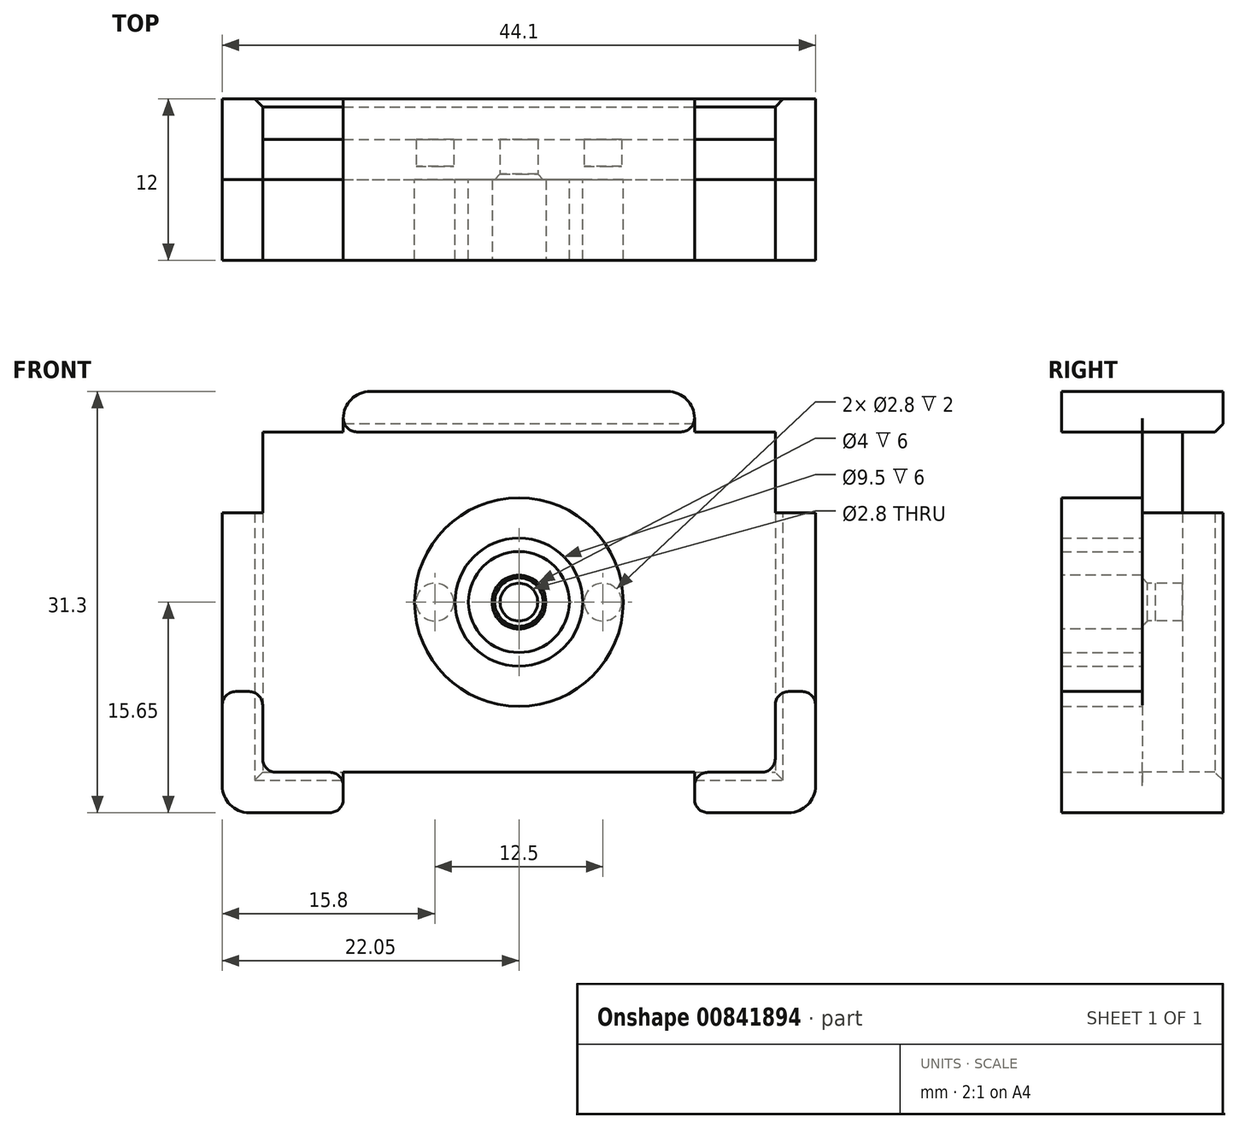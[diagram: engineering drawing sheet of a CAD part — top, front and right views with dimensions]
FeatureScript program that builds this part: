
annotation { "Feature Type Name" : "Feature", "Feature Type Description" : "" }
export const myFeature = defineFeature(function(context is Context, id is Id, definition is map)
    precondition{}
    {
        {
            var Q0;
            Q0=qCreatedBy(makeId("Front.planeOp"),FACE);
            var sketch = newSketch(context, id + "F0", { "sketchPlane" : qUnion([Q0])});
            skLineSegment(sketch, "E0.bottom", {"start": v(-19.05, 12.65) * mm, "end": v(19.05, 12.65) * mm});
            skLineSegment(sketch, "E0.top", {"start": v(-19.05, -12.65) * mm, "end": v(19.05, -12.65) * mm});
            skLineSegment(sketch, "E0.left", {"start": v(-19.05, 12.65) * mm, "end": v(-19.05, -12.65) * mm});
            skLineSegment(sketch, "E0.right", {"start": v(19.05, 12.65) * mm, "end": v(19.05, -12.65) * mm});
            skPoint(sketch, "E0.middle", {"position": v(0, 0) * mm});
            skLineSegment(sketch, "E1.bottom", {"start": v(-22.05, 15.65) * mm, "end": v(22.05, 15.65) * mm});
            skLineSegment(sketch, "E1.top", {"start": v(-22.05, -15.65) * mm, "end": v(22.05, -15.65) * mm});
            skLineSegment(sketch, "E1.left", {"start": v(-22.05, 15.65) * mm, "end": v(-22.05, -15.65) * mm});
            skLineSegment(sketch, "E1.right", {"start": v(22.05, 15.65) * mm, "end": v(22.05, -15.65) * mm});
            skCircle(sketch, "E2", {"center": v(-6.25, 0) * mm, "radius": 1.4 * mm});
            skCircle(sketch, "E3", {"center": v(6.25, 0) * mm, "radius": 1.4 * mm});
            skCircle(sketch, "E4", {"center": v(0, 0) * mm, "radius": 2 * mm});
            skCircle(sketch, "E5", {"center": v(0, 0) * mm, "radius": 4.75 * mm});
            skCircle(sketch, "E6", {"center": v(0, 0) * mm, "radius": 3.75 * mm});
            skCircle(sketch, "E7", {"center": v(0, 0) * mm, "radius": 9.5 * mm});
            skCircle(sketch, "E8", {"center": v(0, 0) * mm, "radius": 7.75 * mm});
            skCircle(sketch, "E9", {"center": v(0, 0) * mm, "radius": 1.4 * mm});
            skLineSegment(sketch, "E10.bottom", {"start": v(-13.05, -12.65) * mm, "end": v(13.05, -12.65) * mm});
            skLineSegment(sketch, "E10.top", {"start": v(-13.05, -15.65) * mm, "end": v(13.05, -15.65) * mm});
            skLineSegment(sketch, "E10.left", {"start": v(-13.05, -12.65) * mm, "end": v(-13.05, -15.65) * mm});
            skLineSegment(sketch, "E10.right", {"start": v(13.05, -12.65) * mm, "end": v(13.05, -15.65) * mm});
            skLineSegment(sketch, "E11.bottom", {"start": v(-13.05, 15.65) * mm, "end": v(13.05, 15.65) * mm});
            skLineSegment(sketch, "E11.top", {"start": v(-13.05, 12.65) * mm, "end": v(13.05, 12.65) * mm});
            skLineSegment(sketch, "E11.left", {"start": v(-13.05, 15.65) * mm, "end": v(-13.05, 12.65) * mm});
            skLineSegment(sketch, "E11.right", {"start": v(13.05, 15.65) * mm, "end": v(13.05, 12.65) * mm});
            skLineSegment(sketch, "E12.bottom", {"start": v(-22.05, -6.65) * mm, "end": v(-19.05, -6.65) * mm});
            skLineSegment(sketch, "E12.top", {"start": v(-22.05, 6.65) * mm, "end": v(-19.05, 6.65) * mm});
            skLineSegment(sketch, "E12.left", {"start": v(-22.05, -6.65) * mm, "end": v(-22.05, 6.65) * mm});
            skLineSegment(sketch, "E12.right", {"start": v(-19.05, -6.65) * mm, "end": v(-19.05, 6.65) * mm});
            skLineSegment(sketch, "E13.bottom", {"start": v(19.05, 6.65) * mm, "end": v(22.05, 6.65) * mm});
            skLineSegment(sketch, "E13.top", {"start": v(19.05, -6.65) * mm, "end": v(22.05, -6.65) * mm});
            skLineSegment(sketch, "E13.left", {"start": v(19.05, 6.65) * mm, "end": v(19.05, -6.65) * mm});
            skLineSegment(sketch, "E13.right", {"start": v(22.05, 6.65) * mm, "end": v(22.05, -6.65) * mm});
            skSolve(sketch);
        }
        {
            var Q0;
            Q0=makeQuery(id+"F0.imprint","IMPRINT",FACE,{"disambiguationData":[TD([[makeQuery(id+"F0.imprint","IMPRINT",EDGE,{"derivedFrom":sQuery(id+"F0.wireOp",EDGE,"E0.bottom")}),-1.0]])]});
            var Q1;
            Q1=makeQuery(id+"F0.imprint","IMPRINT",FACE,{"disambiguationData":[TD([[makeQuery(id+"F0.imprint","IMPRINT",EDGE,{"derivedFrom":sQuery(id+"F0.wireOp",EDGE,"E4")}),-1.0]])]});
            var Q2;
            Q2=makeQuery(id+"F0.imprint","IMPRINT",FACE,{"disambiguationData":[TD([[makeQuery(id+"F0.imprint","IMPRINT",EDGE,{"derivedFrom":sQuery(id+"F0.wireOp",EDGE,"E5")}),1.0]])]});
            var Q3;
            Q3=makeQuery(id+"F0.imprint","IMPRINT",FACE,{"disambiguationData":[TD([[makeQuery(id+"F0.imprint","IMPRINT",EDGE,{"derivedFrom":sQuery(id+"F0.wireOp",EDGE,"E2")}),-1.0]])]});
            var Q4;
            Q4=makeQuery(id+"F0.imprint","IMPRINT",FACE,{"disambiguationData":[TD([[makeQuery(id+"F0.imprint","IMPRINT",EDGE,{"derivedFrom":sQuery(id+"F0.wireOp",EDGE,"E7")}),1.0]])]});
            extrude(context, id + "F1", {"entities" : qUnion([Q0, Q1, Q2, Q3, Q4]), "oppositeDirection" : true, "depth" : 3 * mm, "offsetDistance" : 25 * mm});
        }
        {
            var Q0;
            Q0=makeQuery(id+"F0.imprint","IMPRINT",FACE,{"disambiguationData":[TD([[makeQuery(id+"F0.imprint","IMPRINT",EDGE,{"derivedFrom":sQuery(id+"F0.wireOp",EDGE,"E0.bottom")}),1.0]])]});
            var Q1;
            Q1=makeQuery(id+"F0.imprint","IMPRINT",FACE,{"disambiguationData":[TD([[makeQuery(id+"F0.imprint","IMPRINT",EDGE,{"derivedFrom":sQuery(id+"F0.wireOp",EDGE,"E10.bottom")}),-1.0]])]});
            var Q2;
            Q2=makeQuery(id+"F0.imprint","IMPRINT",FACE,{"disambiguationData":[TD([[makeQuery(id+"F0.imprint","IMPRINT",EDGE,{"derivedFrom":sQuery(id+"F0.wireOp",EDGE,"E11.bottom")}),-1.0]])]});
            var Q3;
            Q3=makeQuery(id+"F0.imprint","IMPRINT",FACE,{"disambiguationData":[TD([[makeQuery(id+"F0.imprint","IMPRINT",EDGE,{"derivedFrom":sQuery(id+"F0.wireOp",EDGE,"E12.bottom")}),1.0]])]});
            var Q4;
            {var subQ7=sQuery(id+"F0.wireOp",EDGE,"E10.left");Q4=makeQuery(id+"F0.imprint","IMPRINT",FACE,{"disambiguationData":[TD([[makeQuery(id+"F0.imprint","IMPRINT",EDGE,{"derivedFrom":subQ7}),-1.0]])]});}
            var Q5;
            {var subQ4=sQuery(id+"F0.wireOp",EDGE,"E10.right");Q5=makeQuery(id+"F0.imprint","IMPRINT",FACE,{"disambiguationData":[TD([[makeQuery(id+"F0.imprint","IMPRINT",EDGE,{"derivedFrom":subQ4}),1.0]])]});}
            var Q6;
            Q6=makeQuery(id+"F0.imprint","IMPRINT",FACE,{"disambiguationData":[TD([[makeQuery(id+"F0.imprint","IMPRINT",EDGE,{"derivedFrom":sQuery(id+"F0.wireOp",EDGE,"E13.bottom")}),-1.0]])]});
            extrude(context, id + "F2", {"entities" : qUnion([Q0, Q1, Q2, Q3, Q4, Q5, Q6]), "operationType" : NewBodyOperationType.ADD, "oppositeDirection" : true, "depth" : 6 * mm, "offsetDistance" : 25 * mm});
        }
        {
            var Q0;
            Q0=makeQuery(id+"F0.imprint","IMPRINT",FACE,{"disambiguationData":[TD([[makeQuery(id+"F0.imprint","IMPRINT",EDGE,{"derivedFrom":sQuery(id+"F0.wireOp",EDGE,"E2")}),1.0]])]});
            var Q1;
            Q1=makeQuery(id+"F0.imprint","IMPRINT",FACE,{"disambiguationData":[TD([[makeQuery(id+"F0.imprint","IMPRINT",EDGE,{"derivedFrom":sQuery(id+"F0.wireOp",EDGE,"E3")}),1.0]])]});
            extrude(context, id + "F3", {"entities" : qUnion([Q0, Q1]), "operationType" : NewBodyOperationType.ADD, "oppositeDirection" : true, "depth" : 1 * mm, "offsetDistance" : 25 * mm});
        }
        {
            var Q0;
            Q0=makeQuery(id+"F0.imprint","IMPRINT",FACE,{"disambiguationData":[TD([[makeQuery(id+"F0.imprint","IMPRINT",EDGE,{"derivedFrom":sQuery(id+"F0.wireOp",EDGE,"E4")}),-1.0]])]});
            extrude(context, id + "F4", {"entities" : qUnion([Q0]), "operationType" : NewBodyOperationType.ADD, "depth" : 6 * mm, "offsetDistance" : 25 * mm});
        }
        {
            var Q0;
            Q0=makeQuery(id+"F0.imprint","IMPRINT",FACE,{"disambiguationData":[TD([[makeQuery(id+"F0.imprint","IMPRINT",EDGE,{"derivedFrom":sQuery(id+"F0.wireOp",EDGE,"E0.bottom")}),1.0]])]});
            var Q1;
            {var subQ7=sQuery(id+"F0.wireOp",EDGE,"E10.left");Q1=makeQuery(id+"F0.imprint","IMPRINT",FACE,{"disambiguationData":[TD([[makeQuery(id+"F0.imprint","IMPRINT",EDGE,{"derivedFrom":subQ7}),-1.0]])]});}
            var Q2;
            {var subQ4=sQuery(id+"F0.wireOp",EDGE,"E10.right");Q2=makeQuery(id+"F0.imprint","IMPRINT",FACE,{"disambiguationData":[TD([[makeQuery(id+"F0.imprint","IMPRINT",EDGE,{"derivedFrom":subQ4}),1.0]])]});}
            extrude(context, id + "F5", {"entities" : qUnion([Q0, Q1, Q2]), "operationType" : NewBodyOperationType.ADD, "depth" : 6 * mm, "offsetDistance" : 25 * mm});
        }
        {
            var Q0;
            Q0=makeQuery(id+"F0.imprint","IMPRINT",FACE,{"disambiguationData":[TD([[makeQuery(id+"F0.imprint","IMPRINT",EDGE,{"derivedFrom":sQuery(id+"F0.wireOp",EDGE,"E2")}),-1.0]])]});
            var Q1;
            Q1=makeQuery(id+"F0.imprint","IMPRINT",FACE,{"disambiguationData":[TD([[makeQuery(id+"F0.imprint","IMPRINT",EDGE,{"derivedFrom":sQuery(id+"F0.wireOp",EDGE,"E2")}),1.0]])]});
            var Q2;
            Q2=makeQuery(id+"F0.imprint","IMPRINT",FACE,{"disambiguationData":[TD([[makeQuery(id+"F0.imprint","IMPRINT",EDGE,{"derivedFrom":sQuery(id+"F0.wireOp",EDGE,"E3")}),1.0]])]});
            extrude(context, id + "F6", {"entities" : qUnion([Q0, Q1, Q2]), "operationType" : NewBodyOperationType.ADD, "depth" : 6 * mm, "offsetDistance" : 25 * mm});
        }
        {
            var Q0;
            Q0=makeQuery(id+"F2.opExtrude","CAP_EDGE",EDGE,{"disambiguationData":[OSD([sQuery(id+"F0.wireOp",EDGE,"E0.bottom")])],"isStart":false});
            var Q1;
            Q1=makeQuery(id+"F2.opExtrude","CAP_EDGE",EDGE,{"disambiguationData":[OSD([sQuery(id+"F0.wireOp",EDGE,"E0.left")])],"isStart":false});
            var Q2;
            Q2=makeQuery(id+"F2.opExtrude","CAP_EDGE",EDGE,{"disambiguationData":[OSD([sQuery(id+"F0.wireOp",EDGE,"E0.right")])],"isStart":false});
            var Q3;
            Q3=makeQuery(id+"F2.opExtrude","CAP_EDGE",EDGE,{"disambiguationData":[OSD([sQuery(id+"F0.wireOp",EDGE,"E0.top")])],"isStart":false});
            chamfer(context, id + "F7", {"entities" : qUnion([Q0, Q1, Q2, Q3]), "width" : 0.6 * mm, "tangentPropagation" : true});
        }
        {
            var Q0;
            Q0=makeQuery(id+"F0.imprint","IMPRINT",FACE,{"disambiguationData":[TD([[makeQuery(id+"F0.imprint","IMPRINT",EDGE,{"derivedFrom":sQuery(id+"F0.wireOp",EDGE,"E4")}),1.0]])]});
            extrude(context, id + "F8", {"entities" : qUnion([Q0]), "operationType" : NewBodyOperationType.ADD, "oppositeDirection" : true, "depth" : 3 * mm, "offsetDistance" : 25 * mm});
        }
        {
            var Q0;
            {var subQ0=sQuery(id+"F0.wireOp",EDGE,"E1.right");var subQ1=sQuery(id+"F0.wireOp",EDGE,"E1.bottom");Q0=makeQuery(id+"F5.boolean.opBoolean","MERGE",EDGE,{"derivedFrom":[makeQuery(id+"F2.opExtrude","SWEPT_EDGE",EDGE,{"disambiguationData":[OSD([subQ1,subQ0])]}),makeQuery(id+"F5.opExtrude","SWEPT_EDGE",EDGE,{"disambiguationData":[OSD([subQ1,subQ0])]})]});}
            var Q1;
            {var subQ0=sQuery(id+"F0.wireOp",EDGE,"E1.left");var subQ1=sQuery(id+"F0.wireOp",EDGE,"E1.bottom");Q1=makeQuery(id+"F5.boolean.opBoolean","MERGE",EDGE,{"derivedFrom":[makeQuery(id+"F2.opExtrude","SWEPT_EDGE",EDGE,{"disambiguationData":[OSD([subQ1,subQ0])]}),makeQuery(id+"F5.opExtrude","SWEPT_EDGE",EDGE,{"disambiguationData":[OSD([subQ1,subQ0])]})]});}
            var Q2;
            {var subQ0=sQuery(id+"F0.wireOp",EDGE,"E1.left");var subQ1=sQuery(id+"F0.wireOp",EDGE,"E1.top");Q2=makeQuery(id+"F5.boolean.opBoolean","MERGE",EDGE,{"derivedFrom":[makeQuery(id+"F2.opExtrude","SWEPT_EDGE",EDGE,{"disambiguationData":[OSD([subQ1,subQ0])]}),makeQuery(id+"F5.opExtrude","SWEPT_EDGE",EDGE,{"disambiguationData":[OSD([subQ1,subQ0])]})]});}
            var Q3;
            {var subQ0=sQuery(id+"F0.wireOp",EDGE,"E1.right");var subQ1=sQuery(id+"F0.wireOp",EDGE,"E1.top");Q3=makeQuery(id+"F5.boolean.opBoolean","MERGE",EDGE,{"derivedFrom":[makeQuery(id+"F2.opExtrude","SWEPT_EDGE",EDGE,{"disambiguationData":[OSD([subQ1,subQ0])]}),makeQuery(id+"F5.opExtrude","SWEPT_EDGE",EDGE,{"disambiguationData":[OSD([subQ1,subQ0])]})]});}
            fillet(context, id + "F9", {"entities" : qUnion([Q0, Q1, Q2, Q3]), "radius" : 2 * mm, "tangentPropagation" : true, "allowEdgeOverflow" : false});
        }
        {
            var Q0;
            Q0=makeQuery(id+"F8.opExtrude","CAP_EDGE",EDGE,{"disambiguationData":[OSD([sQuery(id+"F0.wireOp",EDGE,"E9")])],"isStart":true});
            chamfer(context, id + "F10", {"entities" : qUnion([Q0]), "width" : 0.4 * mm, "tangentPropagation" : true});
        }
        {
            var Q0;
            Q0=makeQuery(id+"F5.opExtrude","SWEPT_EDGE",EDGE,{"disambiguationData":[OSD([sQuery(id+"F0.wireOp",EDGE,"E1.left"),sQuery(id+"F0.wireOp",EDGE,"E12.top"),sQuery(id+"F0.wireOp",EDGE,"E12.left")])]});
            var Q1;
            Q1=makeQuery(id+"F5.opExtrude","SWEPT_EDGE",EDGE,{"disambiguationData":[OSD([sQuery(id+"F0.wireOp",EDGE,"E0.left"),sQuery(id+"F0.wireOp",EDGE,"E12.top"),sQuery(id+"F0.wireOp",EDGE,"E12.right")])]});
            var Q2;
            Q2=makeQuery(id+"F5.opExtrude","SWEPT_EDGE",EDGE,{"disambiguationData":[OSD([sQuery(id+"F0.wireOp",EDGE,"E0.bottom"),sQuery(id+"F0.wireOp",EDGE,"E11.top"),sQuery(id+"F0.wireOp",EDGE,"E11.left")])]});
            var Q3;
            Q3=makeQuery(id+"F5.opExtrude","SWEPT_EDGE",EDGE,{"disambiguationData":[OSD([sQuery(id+"F0.wireOp",EDGE,"E1.bottom"),sQuery(id+"F0.wireOp",EDGE,"E11.bottom"),sQuery(id+"F0.wireOp",EDGE,"E11.left")])]});
            var Q4;
            Q4=makeQuery(id+"F5.opExtrude","SWEPT_EDGE",EDGE,{"disambiguationData":[OSD([sQuery(id+"F0.wireOp",EDGE,"E0.bottom"),sQuery(id+"F0.wireOp",EDGE,"E11.top"),sQuery(id+"F0.wireOp",EDGE,"E11.right")])]});
            var Q5;
            Q5=makeQuery(id+"F5.opExtrude","SWEPT_EDGE",EDGE,{"disambiguationData":[OSD([sQuery(id+"F0.wireOp",EDGE,"E0.right"),sQuery(id+"F0.wireOp",EDGE,"E13.bottom"),sQuery(id+"F0.wireOp",EDGE,"E13.left")])]});
            var Q6;
            Q6=makeQuery(id+"F5.opExtrude","SWEPT_EDGE",EDGE,{"disambiguationData":[OSD([sQuery(id+"F0.wireOp",EDGE,"E1.right"),sQuery(id+"F0.wireOp",EDGE,"E13.bottom"),sQuery(id+"F0.wireOp",EDGE,"E13.right")])]});
            var Q7;
            Q7=makeQuery(id+"F5.opExtrude","SWEPT_EDGE",EDGE,{"disambiguationData":[OSD([sQuery(id+"F0.wireOp",EDGE,"E1.top"),sQuery(id+"F0.wireOp",EDGE,"E10.top"),sQuery(id+"F0.wireOp",EDGE,"E10.left")])]});
            var Q8;
            Q8=makeQuery(id+"F5.opExtrude","SWEPT_EDGE",EDGE,{"disambiguationData":[OSD([sQuery(id+"F0.wireOp",EDGE,"E1.top"),sQuery(id+"F0.wireOp",EDGE,"E10.top"),sQuery(id+"F0.wireOp",EDGE,"E10.right")])]});
            var Q9;
            Q9=makeQuery(id+"F5.opExtrude","SWEPT_EDGE",EDGE,{"disambiguationData":[OSD([sQuery(id+"F0.wireOp",EDGE,"E1.left"),sQuery(id+"F0.wireOp",EDGE,"E12.bottom"),sQuery(id+"F0.wireOp",EDGE,"E12.left")])]});
            var Q10;
            Q10=makeQuery(id+"F5.opExtrude","SWEPT_EDGE",EDGE,{"disambiguationData":[OSD([sQuery(id+"F0.wireOp",EDGE,"E0.left"),sQuery(id+"F0.wireOp",EDGE,"E12.bottom"),sQuery(id+"F0.wireOp",EDGE,"E12.right")])]});
            var Q11;
            Q11=makeQuery(id+"F5.opExtrude","SWEPT_EDGE",EDGE,{"disambiguationData":[OSD([sQuery(id+"F0.wireOp",EDGE,"E1.bottom"),sQuery(id+"F0.wireOp",EDGE,"E11.bottom"),sQuery(id+"F0.wireOp",EDGE,"E11.right")])]});
            var Q12;
            Q12=makeQuery(id+"F5.opExtrude","SWEPT_EDGE",EDGE,{"disambiguationData":[OSD([sQuery(id+"F0.wireOp",EDGE,"E1.right"),sQuery(id+"F0.wireOp",EDGE,"E13.top"),sQuery(id+"F0.wireOp",EDGE,"E13.right")])]});
            var Q13;
            Q13=makeQuery(id+"F5.opExtrude","SWEPT_EDGE",EDGE,{"disambiguationData":[OSD([sQuery(id+"F0.wireOp",EDGE,"E0.right"),sQuery(id+"F0.wireOp",EDGE,"E13.top"),sQuery(id+"F0.wireOp",EDGE,"E13.left")])]});
            var Q14;
            Q14=makeQuery(id+"F5.opExtrude","SWEPT_EDGE",EDGE,{"disambiguationData":[OSD([sQuery(id+"F0.wireOp",EDGE,"E0.top"),sQuery(id+"F0.wireOp",EDGE,"E10.bottom"),sQuery(id+"F0.wireOp",EDGE,"E10.right")])]});
            var Q15;
            Q15=makeQuery(id+"F5.opExtrude","SWEPT_EDGE",EDGE,{"disambiguationData":[OSD([sQuery(id+"F0.wireOp",EDGE,"E0.top"),sQuery(id+"F0.wireOp",EDGE,"E10.bottom"),sQuery(id+"F0.wireOp",EDGE,"E10.left")])]});
            fillet(context, id + "F11", {"entities" : qUnion([Q0, Q1, Q2, Q3, Q4, Q5, Q6, Q7, Q8, Q9, Q10, Q11, Q12, Q13, Q14, Q15]), "radius" : 1 * mm, "tangentPropagation" : true, "allowEdgeOverflow" : false});
        }
    });
